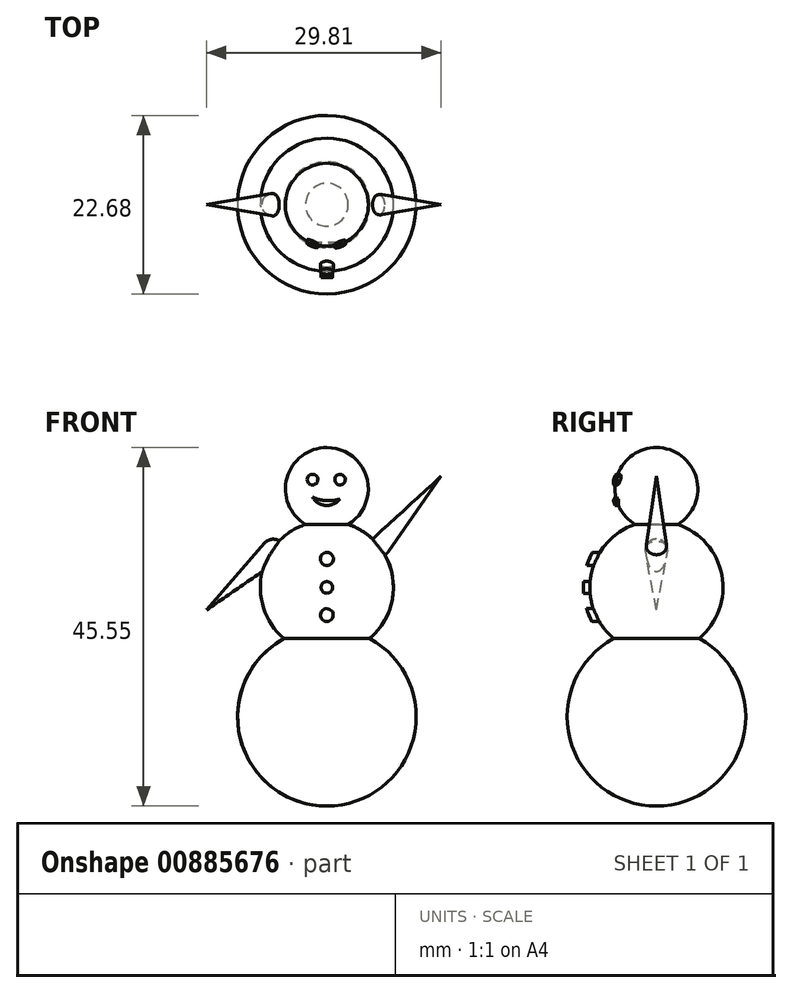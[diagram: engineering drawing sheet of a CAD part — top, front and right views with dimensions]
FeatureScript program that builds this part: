
annotation { "Feature Type Name" : "Feature", "Feature Type Description" : "" }
export const myFeature = defineFeature(function(context is Context, id is Id, definition is map)
    precondition{}
    {
        {
            var Q0;
            Q0=qCreatedBy(makeId("Front.planeOp"),FACE);
            cPlane(context, id + "F0", {"entities" : qUnion([Q0]), "cplaneType" : CPlaneType.OFFSET, "offset" : 50 * mm, "width" : 152.4 * mm, "height" : 152.4 * mm});
        }
        {
            var Q0;
            Q0=qCreatedBy(id+"F0.planeOp",FACE);
            var sketch = newSketch(context, id + "F1", { "sketchPlane" : qUnion([Q0])});
            skCircle(sketch, "E0", {"center": v(-90.2, -23.54) * mm, "radius": 11.34 * mm});
            skCircle(sketch, "E1", {"center": v(-90.2, -7.11) * mm, "radius": 8.46 * mm});
            skCircle(sketch, "E2", {"center": v(-90.2, 5.4) * mm, "radius": 5.26 * mm});
            skLineSegment(sketch, "E3", {"start": v(-90.2, 10.67) * mm, "end": v(-90.2, -34.88) * mm});
            skSolve(sketch);
        }
        {
            var Q0;
            {var subQ0=sQuery(id+"F1.wireOp",EDGE,"E2");var subQ1=sQuery(id+"F1.wireOp",EDGE,"E1");var subQ2=makeQuery(id+"F1.imprint","INTERSECT",VERTEX,{"disambiguationData":[OD(1.0)],"derivedFrom":[subQ1,subQ0]});Q0=makeQuery(id+"F1.imprint","IMPRINT",FACE,{"disambiguationData":[TD([[makeQuery(id+"F1.imprint","IMPRINT",EDGE,{"disambiguationData":[TD([[subQ2,1.0]])],"derivedFrom":subQ1}),-1.0]])]});}
            var Q1;
            {var subQ0=sQuery(id+"F1.wireOp",EDGE,"E2");var subQ1=sQuery(id+"F1.wireOp",EDGE,"E1");var subQ2=makeQuery(id+"F1.imprint","INTERSECT",VERTEX,{"disambiguationData":[OD(1.0)],"derivedFrom":[subQ1,subQ0]});Q1=makeQuery(id+"F1.imprint","IMPRINT",FACE,{"disambiguationData":[TD([[makeQuery(id+"F1.imprint","IMPRINT",EDGE,{"disambiguationData":[TD([[subQ2,1.0]])],"derivedFrom":subQ1}),1.0]])]});}
            var Q2;
            {var subQ0=sQuery(id+"F1.wireOp",EDGE,"E1");var subQ1=sQuery(id+"F1.wireOp",EDGE,"E0");var subQ2=makeQuery(id+"F1.imprint","INTERSECT",VERTEX,{"disambiguationData":[OD(1.0)],"derivedFrom":[subQ1,subQ0]});Q2=makeQuery(id+"F1.imprint","IMPRINT",FACE,{"disambiguationData":[TD([[makeQuery(id+"F1.imprint","IMPRINT",EDGE,{"disambiguationData":[TD([[subQ2,1.0]])],"derivedFrom":subQ1}),-1.0]])]});}
            var Q3;
            {var subQ0=sQuery(id+"F1.wireOp",EDGE,"E1");var subQ1=sQuery(id+"F1.wireOp",EDGE,"E0");var subQ2=makeQuery(id+"F1.imprint","INTERSECT",VERTEX,{"disambiguationData":[OD(1.0)],"derivedFrom":[subQ1,subQ0]});Q3=makeQuery(id+"F1.imprint","IMPRINT",FACE,{"disambiguationData":[TD([[makeQuery(id+"F1.imprint","IMPRINT",EDGE,{"disambiguationData":[TD([[subQ2,1.0]])],"derivedFrom":subQ1}),1.0]])]});}
            var Q4;
            {var subQ0=sQuery(id+"F1.wireOp",EDGE,"E3");var subQ1=sQuery(id+"F1.wireOp",EDGE,"E0");var subQ2=makeQuery(id+"F1.imprint","INTERSECT",VERTEX,{"disambiguationData":[OD(0.0)],"derivedFrom":[subQ1,subQ0]});Q4=makeQuery(id+"F1.imprint","IMPRINT",FACE,{"disambiguationData":[TD([[makeQuery(id+"F1.imprint","IMPRINT",EDGE,{"disambiguationData":[TD([[subQ2,1.0]])],"derivedFrom":subQ1}),1.0]])]});}
            var Q5;
            Q5=sQuery(id+"F1.wireOp",EDGE,"E3");
            revolve(context, id + "F2", {"surfaceOperationType" : NewSurfaceOperationType.NEW, "entities" : qUnion([Q0, Q1, Q2, Q3, Q4]), "axis" : qUnion([Q5]), "revolveType" : RevolveType.FULL});
        }
        {
            var Q0;
            Q0=qCreatedBy(id+"F0.planeOp",FACE);
            var sketch = newSketch(context, id + "F3", { "sketchPlane" : qUnion([Q0])});
            skCircle(sketch, "E4", {"center": v(-97.02, -2.4) * mm, "radius": 1.42 * mm});
            skLineSegment(sketch, "E5", {"start": v(-98.1, -1.47) * mm, "end": v(-105.48, -9.98) * mm});
            skLineSegment(sketch, "E6", {"start": v(-105.48, -9.98) * mm, "end": v(-97.02, -2.4) * mm});
            skLineSegment(sketch, "E7", {"start": v(-97.02, -2.4) * mm, "end": v(-98.1, -1.47) * mm});
            skLineSegment(sketch, "E8", {"start": v(-97.02, -2.4) * mm, "end": v(-95.96, -1.45) * mm});
            skSolve(sketch);
        }
        {
            var Q0;
            {var subQ0=sQuery(id+"F3.wireOp",EDGE,"E5");Q0=makeQuery(id+"F3.imprint","IMPRINT",FACE,{"disambiguationData":[TD([[makeQuery(id+"F3.imprint","IMPRINT",EDGE,{"derivedFrom":subQ0}),1.0]])]});}
            var Q1;
            {var subQ0=sQuery(id+"F3.wireOp",EDGE,"E7");Q1=makeQuery(id+"F3.imprint","IMPRINT",FACE,{"disambiguationData":[TD([[makeQuery(id+"F3.imprint","IMPRINT",EDGE,{"derivedFrom":subQ0}),1.0]])]});}
            var Q2;
            {var subQ0=sQuery(id+"F3.wireOp",EDGE,"E7");Q2=makeQuery(id+"F3.imprint","IMPRINT",FACE,{"disambiguationData":[TD([[makeQuery(id+"F3.imprint","IMPRINT",EDGE,{"derivedFrom":subQ0}),-1.0]])]});}
            var Q3;
            Q3=sQuery(id+"F3.wireOp",EDGE,"E6");
            revolve(context, id + "F4", {"operationType" : NewBodyOperationType.ADD, "surfaceOperationType" : NewSurfaceOperationType.NEW, "entities" : qUnion([Q0, Q1, Q2]), "axis" : qUnion([Q3]), "revolveType" : RevolveType.FULL});
        }
        {
            var Q0;
            Q0=qCreatedBy(id+"F0.planeOp",FACE);
            var sketch = newSketch(context, id + "F5", { "sketchPlane" : qUnion([Q0])});
            skCircle(sketch, "E9", {"center": v(-83.42, -1.81) * mm, "radius": 1.29 * mm});
            skLineSegment(sketch, "E10", {"start": v(-83.42, -1.81) * mm, "end": v(-75.67, 7.02) * mm});
            skLineSegment(sketch, "E11", {"start": v(-75.67, 7.02) * mm, "end": v(-84.3, -0.86) * mm});
            skLineSegment(sketch, "E12", {"start": v(-83.42, -1.81) * mm, "end": v(-84.27, -2.78) * mm});
            skSolve(sketch);
        }
        {
            var Q0;
            {var subQ2=sQuery(id+"F5.wireOp",EDGE,"E12");Q0=makeQuery(id+"F5.imprint","IMPRINT",FACE,{"disambiguationData":[TD([[makeQuery(id+"F5.imprint","IMPRINT",EDGE,{"derivedFrom":subQ2}),-1.0]])]});}
            var Q1;
            {var subQ0=sQuery(id+"F5.wireOp",EDGE,"E11");Q1=makeQuery(id+"F5.imprint","IMPRINT",FACE,{"disambiguationData":[TD([[makeQuery(id+"F5.imprint","IMPRINT",EDGE,{"derivedFrom":subQ0}),1.0]])]});}
            var Q2;
            Q2=sQuery(id+"F5.wireOp",EDGE,"E10");
            revolve(context, id + "F6", {"operationType" : NewBodyOperationType.ADD, "surfaceOperationType" : NewSurfaceOperationType.NEW, "entities" : qUnion([Q0, Q1]), "axis" : qUnion([Q2]), "revolveType" : RevolveType.FULL});
        }
        {
            var Q0;
            Q0=qCreatedBy(id+"F0.planeOp",FACE);
            var sketch = newSketch(context, id + "F7", { "sketchPlane" : qUnion([Q0])});
            skArc(sketch, "E13", {"start": v(-87.48, 0.9) * mm, "mid": v(-90.2, 10.67) * mm, "end": v(-92.9, 0.9) * mm});
            skArc(sketch, "E14", {"start": v(-84.39, -0.96) * mm, "mid": v(-85.83, 0.14) * mm, "end": v(-87.48, 0.9) * mm});
            skArc(sketch, "E15", {"start": v(-92.9, 0.9) * mm, "mid": v(-94.7, 0.04) * mm, "end": v(-96.25, -1.2) * mm});
            skArc(sketch, "E16", {"start": v(-98.4, -5.09) * mm, "mid": v(-98.23, -9.73) * mm, "end": v(-95.63, -13.59) * mm});
            skArc(sketch, "E17", {"start": v(-84.76, -13.59) * mm, "mid": v(-81.87, -8.62) * mm, "end": v(-82.83, -2.96) * mm});
            skArc(sketch, "E18", {"start": v(-95.63, -13.59) * mm, "mid": v(-90.2, -34.88) * mm, "end": v(-84.76, -13.59) * mm});
            skCircle(sketch, "E19", {"center": v(-92.02, 6.59) * mm, "radius": 0.68 * mm});
            skCircle(sketch, "E20", {"center": v(-88.52, 6.59) * mm, "radius": 0.67 * mm});
            skArc(sketch, "E21", {"start": v(-92.02, 4.35) * mm, "mid": v(-90.33, 3.3) * mm, "end": v(-88.52, 4.13) * mm});
            skArc(sketch, "E22", {"start": v(-92.02, 4.35) * mm, "mid": v(-90.29, 3.92) * mm, "end": v(-88.52, 4.13) * mm});
            skSolve(sketch);
        }
        {
            var Q0;
            Q0 = qSketchRegion(id + "F7", true);
            extrude(context, id + "F8", {"entities" : qUnion([Q0]), "operationType" : NewBodyOperationType.ADD, "depth" : 5.5 * mm, "offsetDistance" : 25.4 * mm});
        }
        {
            var Q0;
            Q0=qCreatedBy(id+"F0.planeOp",FACE);
            var sketch = newSketch(context, id + "F9", { "sketchPlane" : qUnion([Q0])});
            skArc(sketch, "E23", {"start": v(-98.4, -5.09) * mm, "mid": v(-98.23, -9.73) * mm, "end": v(-95.63, -13.59) * mm});
            skLineSegment(sketch, "E24", {"start": v(-90.2, 5.4) * mm, "end": v(-90.21, 12.07) * mm});
            skPoint(sketch, "E25", {"position": v(-90.21, 12.07) * mm});
            skLineSegment(sketch, "E26", {"start": v(-86.32, 1.28) * mm, "end": v(-85.34, 0.84) * mm});
            skCircle(sketch, "E27", {"center": v(-90.2, 5.4) * mm, "radius": 5.66 * mm});
            skCircle(sketch, "E28", {"center": v(-90.2, 5.4) * mm, "radius": 6.66 * mm});
            skSolve(sketch);
        }
        {
            var Q0;
            {var subQ0=sQuery(id+"F9.wireOp",EDGE,"E26");Q0=makeQuery(id+"F9.imprint","IMPRINT",FACE,{"disambiguationData":[TD([[makeQuery(id+"F9.imprint","IMPRINT",EDGE,{"derivedFrom":subQ0}),1.0]])]});}
            var Q1;
            Q1=sQuery(id+"F9.wireOp",EDGE,"E24");
            revolve(context, id + "F10", {"operationType" : NewBodyOperationType.REMOVE, "surfaceOperationType" : NewSurfaceOperationType.NEW, "entities" : qUnion([Q0]), "axis" : qUnion([Q1]), "revolveType" : RevolveType.FULL, "oppositeDirection" : true});
        }
        {
            var Q0;
            Q0=qCreatedBy(id+"F0.planeOp",FACE);
            var sketch = newSketch(context, id + "F11", { "sketchPlane" : qUnion([Q0])});
            skArc(sketch, "E29", {"start": v(-84.39, -0.96) * mm, "mid": v(-85.83, 0.14) * mm, "end": v(-87.48, 0.9) * mm});
            skArc(sketch, "E30", {"start": v(-92.9, 0.9) * mm, "mid": v(-94.7, 0.04) * mm, "end": v(-96.25, -1.2) * mm});
            skArc(sketch, "E31", {"start": v(-98.4, -5.09) * mm, "mid": v(-98.23, -9.73) * mm, "end": v(-95.63, -13.59) * mm});
            skArc(sketch, "E32", {"start": v(-84.76, -13.59) * mm, "mid": v(-81.87, -8.62) * mm, "end": v(-82.83, -2.96) * mm});
            skArc(sketch, "E33", {"start": v(-95.63, -13.59) * mm, "mid": v(-90.2, -34.88) * mm, "end": v(-84.76, -13.59) * mm});
            skCircle(sketch, "E34", {"center": v(-90.2, -3.47) * mm, "radius": 0.84 * mm});
            skCircle(sketch, "E35", {"center": v(-90.2, -7.11) * mm, "radius": 0.74 * mm});
            skCircle(sketch, "E36", {"center": v(-90.2, -10.62) * mm, "radius": 0.82 * mm});
            skSolve(sketch);
        }
        {
            var Q0;
            Q0 = qSketchRegion(id + "F11", true);
            extrude(context, id + "F12", {"entities" : qUnion([Q0]), "operationType" : NewBodyOperationType.ADD, "depth" : 10.16 * mm, "offsetDistance" : 25.4 * mm});
        }
        {
            var Q0;
            Q0=qCreatedBy(id+"F0.planeOp",FACE);
            var sketch = newSketch(context, id + "F13", { "sketchPlane" : qUnion([Q0])});
            skArc(sketch, "E37", {"start": v(-84.39, -0.96) * mm, "mid": v(-85.83, 0.14) * mm, "end": v(-87.48, 0.9) * mm});
            skArc(sketch, "E38", {"start": v(-92.9, 0.9) * mm, "mid": v(-94.7, 0.04) * mm, "end": v(-96.25, -1.2) * mm});
            skArc(sketch, "E39", {"start": v(-98.4, -5.09) * mm, "mid": v(-98.23, -9.73) * mm, "end": v(-95.63, -13.59) * mm});
            skArc(sketch, "E40", {"start": v(-84.76, -13.59) * mm, "mid": v(-81.87, -8.62) * mm, "end": v(-82.83, -2.96) * mm});
            skCircle(sketch, "E41", {"center": v(-90.2, -7.11) * mm, "radius": 8.46 * mm});
            skCircle(sketch, "E42", {"center": v(-90.2, -7.11) * mm, "radius": 9.28 * mm});
            skCircle(sketch, "E43", {"center": v(-90.2, -7.11) * mm, "radius": 11.57 * mm});
            skLineSegment(sketch, "E44", {"start": v(-90.2, -7.11) * mm, "end": v(-90.2, 4.46) * mm});
            skLineSegment(sketch, "E45", {"start": v(-90.2, 4.46) * mm, "end": v(-90.2, -18.68) * mm});
            skLineSegment(sketch, "E46", {"start": v(-90.2, -2.9) * mm, "end": v(-79.4, -2.96) * mm});
            skLineSegment(sketch, "E47", {"start": v(-83.55, -13.59) * mm, "end": v(-81.95, -15.23) * mm});
            skLineSegment(sketch, "E48", {"start": v(-75.67, 7.02) * mm, "end": v(-82.37, -2.55) * mm});
            skLineSegment(sketch, "E49", {"start": v(-84.3, -0.86) * mm, "end": v(-75.67, 7.02) * mm});
            skSolve(sketch);
        }
        {
            var Q0;
            {var subQ0=sQuery(id+"F13.wireOp",EDGE,"E47");Q0=makeQuery(id+"F13.imprint","IMPRINT",FACE,{"disambiguationData":[TD([[makeQuery(id+"F13.imprint","IMPRINT",EDGE,{"derivedFrom":subQ0}),1.0]])]});}
            var Q1;
            {var subQ0=sQuery(id+"F13.wireOp",EDGE,"E48");var subQ1=sQuery(id+"F13.wireOp",EDGE,"E42");var subQ2=makeQuery(id+"F13.imprint","INTERSECT",VERTEX,{"derivedFrom":[subQ1,subQ0]});Q1=makeQuery(id+"F13.imprint","IMPRINT",FACE,{"disambiguationData":[TD([[makeQuery(id+"F13.imprint","IMPRINT",EDGE,{"disambiguationData":[TD([[subQ2,1.0]])],"derivedFrom":subQ1}),-1.0]])]});}
            var Q2;
            Q2=sQuery(id+"F13.wireOp",EDGE,"E45");
            revolve(context, id + "F14", {"operationType" : NewBodyOperationType.REMOVE, "surfaceOperationType" : NewSurfaceOperationType.NEW, "entities" : qUnion([Q0, Q1]), "axis" : qUnion([Q2]), "revolveType" : RevolveType.ONE_DIRECTION, "angle" : 110 * degree});
        }
        {
            var Q0;
            {var subQ5=sQuery(id+"F9.wireOp",EDGE,"E26");Q0=makeQuery(id+"F9.imprint","IMPRINT",FACE,{"disambiguationData":[TD([[makeQuery(id+"F9.imprint","IMPRINT",EDGE,{"derivedFrom":subQ5}),1.0]])]});}
            var Q1;
            Q1=sQuery(id+"F9.wireOp",EDGE,"E24");
            revolve(context, id + "F15", {"operationType" : NewBodyOperationType.REMOVE, "surfaceOperationType" : NewSurfaceOperationType.NEW, "entities" : qUnion([Q0]), "axis" : qUnion([Q1]), "revolveType" : RevolveType.FULL, "oppositeDirection" : true});
        }
    });
